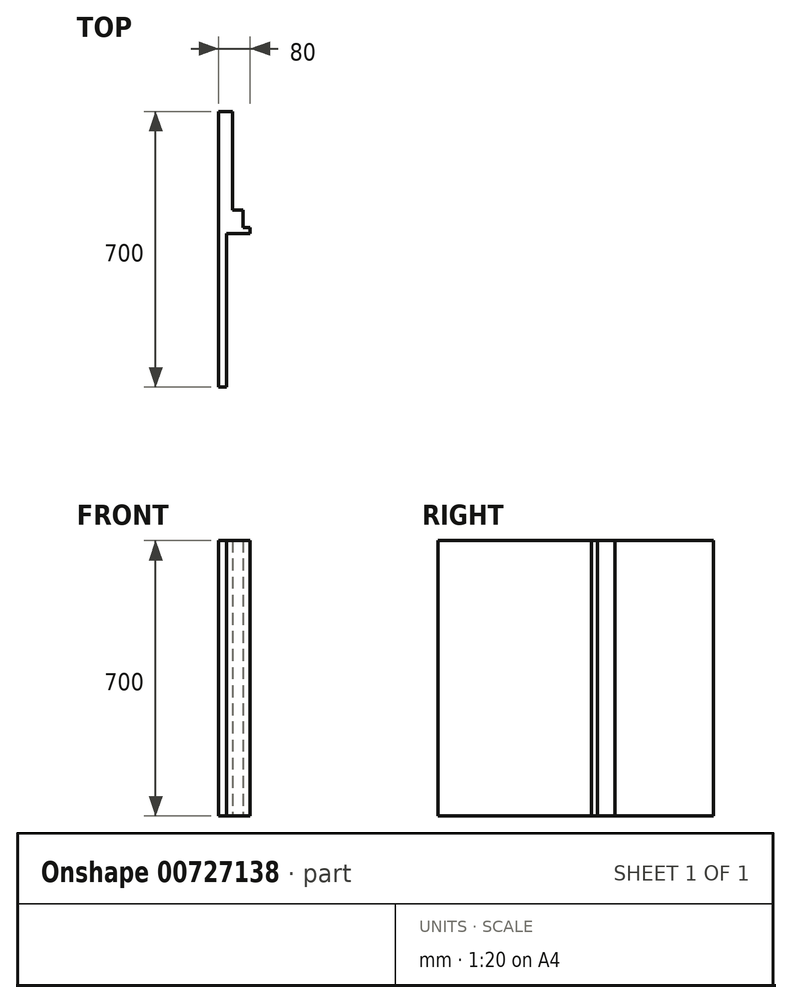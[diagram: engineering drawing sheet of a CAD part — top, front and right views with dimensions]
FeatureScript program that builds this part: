
annotation { "Feature Type Name" : "Feature", "Feature Type Description" : "" }
export const myFeature = defineFeature(function(context is Context, id is Id, definition is map)
    precondition{}
    {
        {
            var Q0;
            Q0=qCreatedBy(makeId("Top.planeOp"),FACE);
            var sketch = newSketch(context, id + "F0", { "sketchPlane" : qUnion([Q0])});
            skLineSegment(sketch, "E0", {"start": v(0, 310) * mm, "end": v(0, 60) * mm});
            skLineSegment(sketch, "E1", {"start": v(0, 60) * mm, "end": v(27, 60) * mm});
            skLineSegment(sketch, "E2", {"start": v(27, 60) * mm, "end": v(27, 15) * mm});
            skLineSegment(sketch, "E3", {"start": v(27, 15) * mm, "end": v(45, 15) * mm});
            skLineSegment(sketch, "E4", {"start": v(45, 15) * mm, "end": v(45, 0) * mm});
            skLineSegment(sketch, "E5", {"start": v(45, 0) * mm, "end": v(-15, 0) * mm});
            skLineSegment(sketch, "E6", {"start": v(-15, 0) * mm, "end": v(-15, -390) * mm});
            skLineSegment(sketch, "E7", {"start": v(-15, -390) * mm, "end": v(-35, -390) * mm});
            skLineSegment(sketch, "E8", {"start": v(-35, -390) * mm, "end": v(-35, 310) * mm});
            skLineSegment(sketch, "E9", {"start": v(-35, 310) * mm, "end": v(0, 310) * mm});
            skSolve(sketch);
        }
        {
            var Q0;
            Q0 = qSketchRegion(id + "F0", true);
            extrude(context, id + "F1", {"entities" : qUnion([Q0]), "endBound" : BoundingType.SYMMETRIC, "depth" : 700 * mm, "offsetDistance" : 25 * mm});
        }
    });
